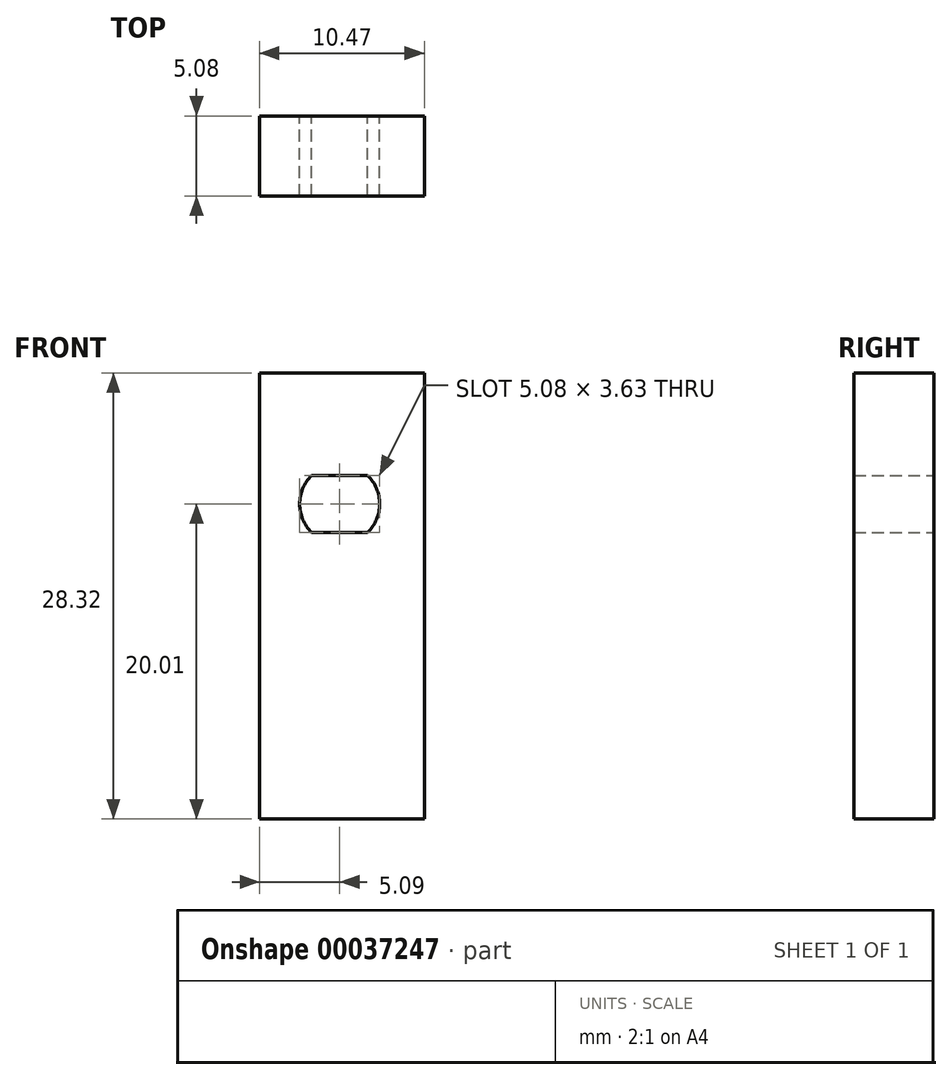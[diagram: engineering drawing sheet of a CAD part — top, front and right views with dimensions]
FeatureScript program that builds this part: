
annotation { "Feature Type Name" : "Feature", "Feature Type Description" : "" }
export const myFeature = defineFeature(function(context is Context, id is Id, definition is map)
    precondition{}
    {
        {
            var Q0;
            Q0=qCreatedBy(makeId("Front.planeOp"),FACE);
            var sketch = newSketch(context, id + "F0", { "sketchPlane" : qUnion([Q0])});
            skPoint(sketch, "E0.rect.middle", {"position": v(0, 0) * mm});
            skCircle(sketch, "E1", {"center": v(0, 0) * mm, "radius": 2.54 * mm});
            skLineSegment(sketch, "E2.rect.bottom", {"start": v(1.78, 1.81) * mm, "end": v(-1.78, 1.81) * mm});
            skLineSegment(sketch, "E2.rect.top", {"start": v(1.78, -1.81) * mm, "end": v(-1.78, -1.81) * mm});
            skLineSegment(sketch, "E2.rect.left", {"start": v(1.78, 1.81) * mm, "end": v(1.78, -1.81) * mm});
            skLineSegment(sketch, "E2.rect.right", {"start": v(-1.78, 1.81) * mm, "end": v(-1.78, -1.81) * mm});
            skLineSegment(sketch, "E3.bottom", {"start": v(-5.09, -20) * mm, "end": v(5.38, -20) * mm});
            skLineSegment(sketch, "E3.top", {"start": v(-5.09, 8.3) * mm, "end": v(5.38, 8.3) * mm});
            skLineSegment(sketch, "E3.left", {"start": v(-5.09, -20) * mm, "end": v(-5.09, 8.3) * mm});
            skLineSegment(sketch, "E3.right", {"start": v(5.38, -20) * mm, "end": v(5.38, 8.3) * mm});
            skLineSegment(sketch, "E4", {"start": v(-5.09, 0) * mm, "end": v(5.38, 0) * mm, "construction": true});
            skSolve(sketch);
        }
        {
            var Q0;
            Q0=makeQuery(id+"F0.imprint","IMPRINT",FACE,{"disambiguationData":[TD([[makeQuery(id+"F0.imprint","IMPRINT",EDGE,{"derivedFrom":sQuery(id+"F0.wireOp",EDGE,"E3.bottom")}),1.0]])]});
            var Q1;
            {var subQ0=sQuery(id+"F0.wireOp",EDGE,"E2.rect.bottom");Q1=makeQuery(id+"F0.imprint","IMPRINT",FACE,{"disambiguationData":[TD([[makeQuery(id+"F0.imprint","IMPRINT",EDGE,{"derivedFrom":subQ0}),-1.0]])]});}
            var Q2;
            {var subQ0=sQuery(id+"F0.wireOp",EDGE,"E2.rect.top");Q2=makeQuery(id+"F0.imprint","IMPRINT",FACE,{"disambiguationData":[TD([[makeQuery(id+"F0.imprint","IMPRINT",EDGE,{"derivedFrom":subQ0}),1.0]])]});}
            extrude(context, id + "F1", {"entities" : qUnion([Q0, Q1, Q2]), "depth" : 5.08 * mm});
        }
    });
